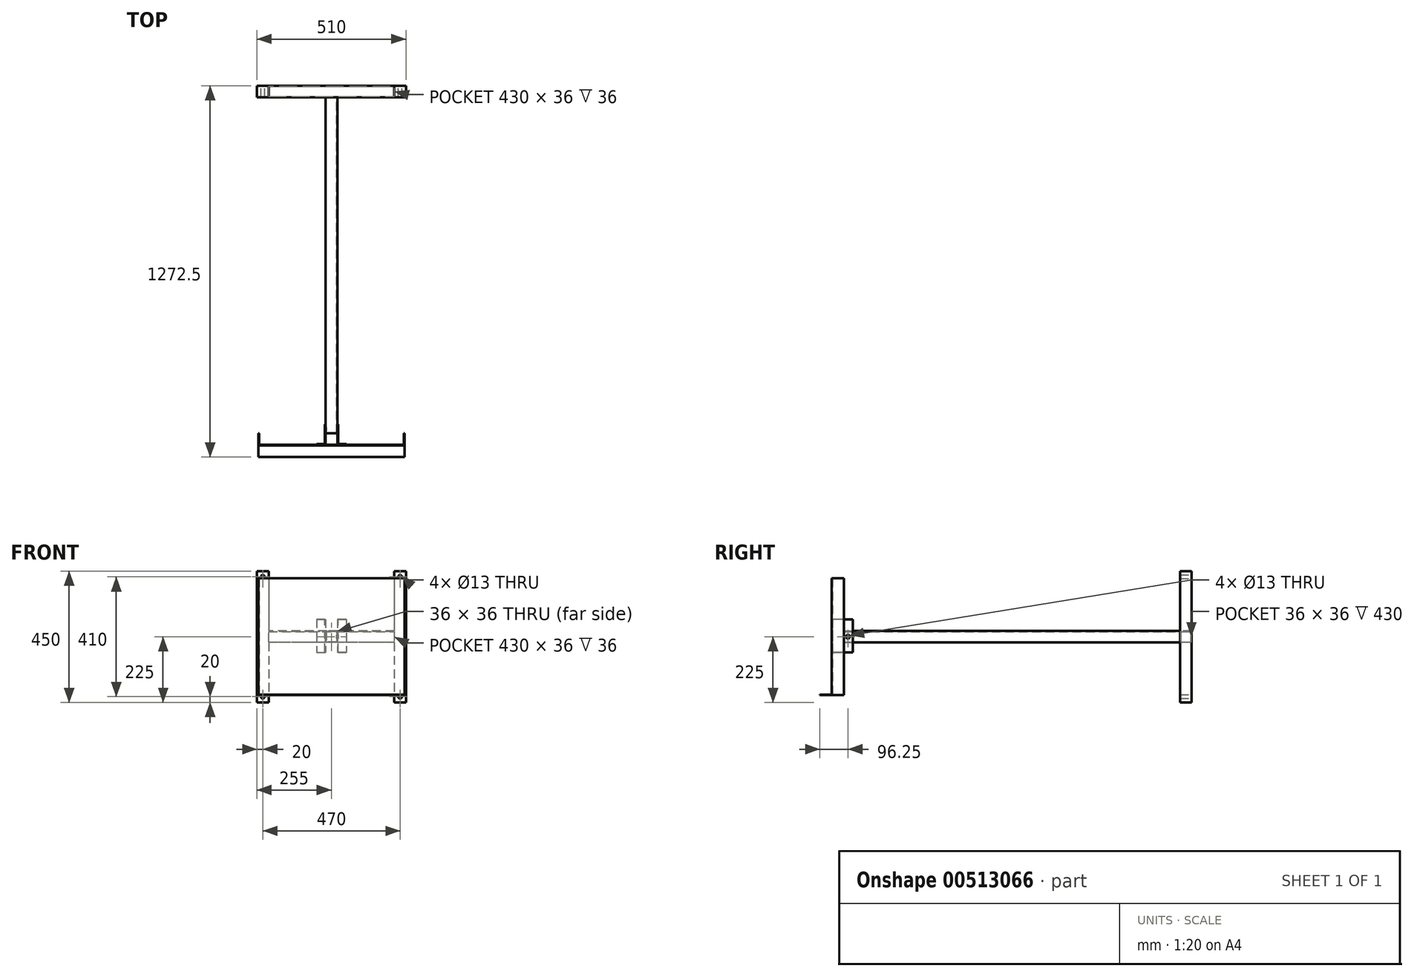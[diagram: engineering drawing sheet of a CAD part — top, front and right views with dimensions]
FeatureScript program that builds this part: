
annotation { "Feature Type Name" : "Feature", "Feature Type Description" : "" }
export const myFeature = defineFeature(function(context is Context, id is Id, definition is map)
    precondition{}
    {
        {
            var Q0;
            Q0=qCreatedBy(makeId("Front.planeOp"),FACE);
            var sketch = newSketch(context, id + "F0", { "sketchPlane" : qUnion([Q0])});
            skLineSegment(sketch, "E0.bottom", {"start": v(-250, 200) * mm, "end": v(250, 200) * mm});
            skLineSegment(sketch, "E0.top", {"start": v(-250, -200) * mm, "end": v(250, -200) * mm});
            skLineSegment(sketch, "E0.left", {"start": v(-250, 200) * mm, "end": v(-250, -200) * mm});
            skLineSegment(sketch, "E0.right", {"start": v(250, 200) * mm, "end": v(250, -200) * mm});
            skPoint(sketch, "E0.middle", {"position": v(0, 0) * mm});
            skSolve(sketch);
        }
        {
            var Q0;
            Q0 = qSketchRegion(id + "F0", true);
            extrude(context, id + "F1", {"entities" : qUnion([Q0]), "depth" : 2.5 * mm, "offsetDistance" : 25 * mm});
        }
        {
            var Q0;
            Q0=makeQuery(id+"F1.opExtrude","CAP_FACE",FACE,{"disambiguationData":[OSD([sQuery(id+"F0.wireOp",EDGE,"E0.bottom"),sQuery(id+"F0.wireOp",EDGE,"E0.top"),sQuery(id+"F0.wireOp",EDGE,"E0.left"),sQuery(id+"F0.wireOp",EDGE,"E0.right")])],"isStart":false});
            var sketch = newSketch(context, id + "F2", { "sketchPlane" : qUnion([Q0])});
            skLineSegment(sketch, "E1.bottom", {"start": v(-250, -198) * mm, "end": v(250, -198) * mm});
            skLineSegment(sketch, "E1.top", {"start": v(-250, -200) * mm, "end": v(250, -200) * mm});
            skLineSegment(sketch, "E1.left", {"start": v(-250, -198) * mm, "end": v(-250, -200) * mm});
            skLineSegment(sketch, "E1.right", {"start": v(250, -198) * mm, "end": v(250, -200) * mm});
            skSolve(sketch);
        }
        {
            var Q0;
            Q0=makeQuery(id+"F2.imprint","IMPRINT",FACE,{"disambiguationData":[TD([[makeQuery(id+"F2.imprint","IMPRINT",EDGE,{"derivedFrom":sQuery(id+"F2.wireOp",EDGE,"E1.bottom")}),-1.0]])]});
            extrude(context, id + "F3", {"entities" : qUnion([Q0]), "operationType" : NewBodyOperationType.ADD, "depth" : 40 * mm, "offsetDistance" : 25 * mm});
        }
        {
            var Q0;
            Q0=makeQuery(id+"F1.opExtrude","CAP_FACE",FACE,{"disambiguationData":[OSD([sQuery(id+"F0.wireOp",EDGE,"E0.bottom"),sQuery(id+"F0.wireOp",EDGE,"E0.top"),sQuery(id+"F0.wireOp",EDGE,"E0.left"),sQuery(id+"F0.wireOp",EDGE,"E0.right")])],"isStart":true});
            var sketch = newSketch(context, id + "F4", { "sketchPlane" : qUnion([Q0])});
            skLineSegment(sketch, "E2.bottom", {"start": v(-250, 200) * mm, "end": v(-248, 200) * mm});
            skLineSegment(sketch, "E2.top", {"start": v(-250, -200) * mm, "end": v(-248, -200) * mm});
            skLineSegment(sketch, "E2.left", {"start": v(-250, 200) * mm, "end": v(-250, -200) * mm});
            skLineSegment(sketch, "E2.right", {"start": v(-248, 200) * mm, "end": v(-248, -200) * mm});
            skLineSegment(sketch, "E3", {"start": v(0, 0) * mm, "end": v(0, 200) * mm, "construction": true});
            skLineSegment(sketch, "E4.MirrorCS", {"start": v(250, 200) * mm, "end": v(248, 200) * mm});
            skLineSegment(sketch, "E5.MirrorCS", {"start": v(250, -200) * mm, "end": v(248, -200) * mm});
            skLineSegment(sketch, "E6.MirrorCS", {"start": v(250, 200) * mm, "end": v(250, -200) * mm});
            skLineSegment(sketch, "E7.MirrorCS", {"start": v(248, 200) * mm, "end": v(248, -200) * mm});
            skSolve(sketch);
        }
        {
            var Q0;
            Q0=makeQuery(id+"F4.imprint","IMPRINT",FACE,{"disambiguationData":[TD([[makeQuery(id+"F4.imprint","IMPRINT",EDGE,{"derivedFrom":sQuery(id+"F4.wireOp",EDGE,"E2.bottom")}),1.0]])]});
            var Q1;
            Q1=makeQuery(id+"F4.imprint","IMPRINT",FACE,{"disambiguationData":[TD([[makeQuery(id+"F4.imprint","IMPRINT",EDGE,{"derivedFrom":sQuery(id+"F4.wireOp",EDGE,"E4.MirrorCS")}),1.0]])]});
            extrude(context, id + "F5", {"entities" : qUnion([Q0, Q1]), "operationType" : NewBodyOperationType.ADD, "depth" : 40 * mm, "offsetDistance" : 25 * mm});
        }
        {
            var Q0;
            Q0=makeQuery(id+"F1.opExtrude","CAP_FACE",FACE,{"disambiguationData":[OSD([sQuery(id+"F0.wireOp",EDGE,"E0.bottom"),sQuery(id+"F0.wireOp",EDGE,"E0.top"),sQuery(id+"F0.wireOp",EDGE,"E0.left"),sQuery(id+"F0.wireOp",EDGE,"E0.right")])],"isStart":true});
            var sketch = newSketch(context, id + "F6", { "sketchPlane" : qUnion([Q0])});
            skLineSegment(sketch, "E8", {"start": v(0, 224.2) * mm, "end": v(0, 0) * mm, "construction": true});
            skLineSegment(sketch, "E9", {"start": v(0, 0) * mm, "end": v(-292.5, 0) * mm, "construction": true});
            skLineSegment(sketch, "E10.bottom", {"start": v(-50.5, 60) * mm, "end": v(-20.5, 60) * mm});
            skLineSegment(sketch, "E10.top", {"start": v(-50.5, -53.15) * mm, "end": v(-20.5, -53.15) * mm});
            skLineSegment(sketch, "E10.left", {"start": v(-50.5, 60) * mm, "end": v(-50.5, -53.15) * mm});
            skLineSegment(sketch, "E10.right", {"start": v(-20.5, 60) * mm, "end": v(-20.5, -53.15) * mm});
            skLineSegment(sketch, "E11.MirrorCS", {"start": v(50.5, -53.15) * mm, "end": v(20.5, -53.15) * mm});
            skLineSegment(sketch, "E12.MirrorCS", {"start": v(50.5, 60) * mm, "end": v(20.5, 60) * mm});
            skLineSegment(sketch, "E13.MirrorCS", {"start": v(20.5, 60) * mm, "end": v(20.5, -53.15) * mm});
            skLineSegment(sketch, "E14.MirrorCS", {"start": v(50.5, 60) * mm, "end": v(50.5, -53.15) * mm});
            skSolve(sketch);
        }
        {
            var Q0;
            Q0=makeQuery(id+"F6.imprint","IMPRINT",FACE,{"disambiguationData":[TD([[makeQuery(id+"F6.imprint","IMPRINT",EDGE,{"derivedFrom":sQuery(id+"F6.wireOp",EDGE,"E10.bottom")}),-1.0]])]});
            var Q1;
            Q1=makeQuery(id+"F6.imprint","IMPRINT",FACE,{"disambiguationData":[TD([[makeQuery(id+"F6.imprint","IMPRINT",EDGE,{"derivedFrom":sQuery(id+"F6.wireOp",EDGE,"E11.MirrorCS")}),-1.0]])]});
            extrude(context, id + "F7", {"entities" : qUnion([Q0, Q1]), "operationType" : NewBodyOperationType.ADD, "depth" : 70 * mm, "offsetDistance" : 25 * mm});
        }
        {
            var Q0;
            Q0=makeQuery(id+"F7.opExtrude","SWEPT_FACE",FACE,{"disambiguationData":[OSD([sQuery(id+"F6.wireOp",EDGE,"E12.MirrorCS")])]});
            var sketch = newSketch(context, id + "F8", { "sketchPlane" : qUnion([Q0])});
            skLineSegment(sketch, "E15", {"start": v(0, 0) * mm, "end": v(0, 112.26) * mm, "construction": true});
            skLineSegment(sketch, "E16", {"start": v(-22.5, 70) * mm, "end": v(-22.5, 2) * mm});
            skLineSegment(sketch, "E17", {"start": v(-22.5, 2) * mm, "end": v(-50.5, 2) * mm});
            skLineSegment(sketch, "E18", {"start": v(-22.5, 70) * mm, "end": v(-20.5, 70) * mm});
            skLineSegment(sketch, "E19", {"start": v(-20.5, 70) * mm, "end": v(-20.5, 0) * mm});
            skLineSegment(sketch, "E20", {"start": v(-20.5, 0) * mm, "end": v(-50.5, 0) * mm});
            skLineSegment(sketch, "E21", {"start": v(-50.5, 0) * mm, "end": v(-50.5, 2) * mm});
            skLineSegment(sketch, "E22", {"start": v(-22.5, 70) * mm, "end": v(-50.5, 70) * mm});
            skLineSegment(sketch, "E23", {"start": v(-50.5, 70) * mm, "end": v(-50.5, 2) * mm});
            skLineSegment(sketch, "E24.MirrorCS", {"start": v(50.5, 0) * mm, "end": v(50.5, 2) * mm});
            skLineSegment(sketch, "E25.MirrorCS", {"start": v(22.5, 70) * mm, "end": v(20.5, 70) * mm});
            skLineSegment(sketch, "E26.MirrorCS", {"start": v(50.5, 70) * mm, "end": v(50.5, 2) * mm});
            skLineSegment(sketch, "E27.MirrorCS", {"start": v(22.5, 70) * mm, "end": v(50.5, 70) * mm});
            skLineSegment(sketch, "E28.MirrorCS", {"start": v(22.5, 70) * mm, "end": v(22.5, 2) * mm});
            skLineSegment(sketch, "E29.MirrorCS", {"start": v(20.5, 0) * mm, "end": v(50.5, 0) * mm});
            skLineSegment(sketch, "E30.MirrorCS", {"start": v(22.5, 2) * mm, "end": v(50.5, 2) * mm});
            skLineSegment(sketch, "E31.MirrorCS", {"start": v(20.5, 70) * mm, "end": v(20.5, 0) * mm});
            skSolve(sketch);
        }
        {
            var Q0;
            Q0=makeQuery(id+"F8.imprint","IMPRINT",FACE,{"disambiguationData":[TD([[makeQuery(id+"F8.imprint","IMPRINT",EDGE,{"derivedFrom":sQuery(id+"F8.wireOp",EDGE,"E26.MirrorCS")}),-1.0]])]});
            var Q1;
            Q1=makeQuery(id+"F8.imprint","IMPRINT",FACE,{"disambiguationData":[TD([[makeQuery(id+"F8.imprint","IMPRINT",EDGE,{"derivedFrom":sQuery(id+"F8.wireOp",EDGE,"E16")}),-1.0]])]});
            extrude(context, id + "F9", {"entities" : qUnion([Q0, Q1]), "operationType" : NewBodyOperationType.REMOVE, "endBound" : BoundingType.THROUGH_ALL, "oppositeDirection" : true, "depth" : 25 * mm, "offsetDistance" : 25 * mm});
        }
        {
            var Q0;
            Q0=qCreatedBy(makeId("Top.planeOp"),FACE);
            cPlane(context, id + "F10", {"entities" : qUnion([Q0]), "cplaneType" : CPlaneType.OFFSET, "offset" : 20 * mm, "width" : 150 * mm, "height" : 150 * mm});
        }
        {
            var Q0;
            Q0=qCreatedBy(id+"F10.planeOp",FACE);
            var sketch = newSketch(context, id + "F11", { "sketchPlane" : qUnion([Q0])});
            skLineSegment(sketch, "E32", {"start": v(0, 0) * mm, "end": v(0, -50.27) * mm, "construction": true});
            skLineSegment(sketch, "E33.bottom", {"start": v(0, 40) * mm, "end": v(20, 40) * mm});
            skLineSegment(sketch, "E33.top", {"start": v(0, 1190) * mm, "end": v(20, 1190) * mm});
            skLineSegment(sketch, "E33.right", {"start": v(20, 40) * mm, "end": v(20, 1190) * mm});
            skLineSegment(sketch, "E34.MirrorCS", {"start": v(-20, 40) * mm, "end": v(-20, 1190) * mm});
            skLineSegment(sketch, "E35.MirrorCS", {"start": v(0, 40) * mm, "end": v(-20, 40) * mm});
            skLineSegment(sketch, "E36.MirrorCS", {"start": v(0, 1190) * mm, "end": v(-20, 1190) * mm});
            skSolve(sketch);
        }
        {
            var Q0;
            Q0 = qSketchRegion(id + "F11", true);
            extrude(context, id + "F12", {"entities" : qUnion([Q0]), "oppositeDirection" : true, "depth" : 40 * mm, "offsetDistance" : 25 * mm});
        }
        {
            var Q0;
            Q0=makeQuery(id+"F12.opExtrude","SWEPT_FACE",FACE,{"disambiguationData":[OSD([sQuery(id+"F11.wireOp",EDGE,"E33.top"),sQuery(id+"F11.wireOp",EDGE,"E36.MirrorCS")])]});
            var sketch = newSketch(context, id + "F13", { "sketchPlane" : qUnion([Q0])});
            skLineSegment(sketch, "E37.bottom", {"start": v(-18, 18) * mm, "end": v(18, 18) * mm});
            skLineSegment(sketch, "E37.top", {"start": v(-18, -18) * mm, "end": v(18, -18) * mm});
            skLineSegment(sketch, "E37.left", {"start": v(-18, 18) * mm, "end": v(-18, -18) * mm});
            skLineSegment(sketch, "E37.right", {"start": v(18, 18) * mm, "end": v(18, -18) * mm});
            skPoint(sketch, "E37.middle", {"position": v(0, 0) * mm});
            skSolve(sketch);
        }
        {
            var Q0;
            Q0=makeQuery(id+"F13.imprint","IMPRINT",FACE,{"disambiguationData":[TD([[makeQuery(id+"F13.imprint","IMPRINT",EDGE,{"derivedFrom":sQuery(id+"F13.wireOp",EDGE,"E37.bottom")}),-1.0]])]});
            extrude(context, id + "F14", {"entities" : qUnion([Q0]), "operationType" : NewBodyOperationType.REMOVE, "oppositeDirection" : true, "depth" : 1151 * mm, "offsetDistance" : 25 * mm});
        }
        {
            var Q0;
            Q0=makeQuery(id+"F9.boolean.opBoolean","COPY",FACE,{"derivedFrom":makeQuery(id+"F9.opExtrude","SWEPT_FACE",FACE,{"disambiguationData":[OSD([sQuery(id+"F8.wireOp",EDGE,"E16")])]})});
            var sketch = newSketch(context, id + "F15", { "sketchPlane" : qUnion([Q0])});
            skLineSegment(sketch, "E38.bottom", {"start": v(-70, 20) * mm, "end": v(2.5, 20) * mm});
            skLineSegment(sketch, "E38.left", {"start": v(2.5, 20) * mm, "end": v(2.5, 0) * mm});
            skLineSegment(sketch, "E38.right", {"start": v(-70, 20) * mm, "end": v(-70, 0) * mm});
            skLineSegment(sketch, "E39.MirrorCS", {"start": v(-30, -20) * mm, "end": v(-37.5, -20) * mm});
            skLineSegment(sketch, "E40", {"start": v(0, 0) * mm, "end": v(-67.93, 0) * mm, "construction": true});
            skLineSegment(sketch, "E41.MirrorCS", {"start": v(-70, -20) * mm, "end": v(-70, 0) * mm});
            skLineSegment(sketch, "E42.MirrorCS", {"start": v(2.5, -20) * mm, "end": v(2.5, 0) * mm});
            skLineSegment(sketch, "E43", {"start": v(-70, 20) * mm, "end": v(-37.5, -20) * mm});
            skLineSegment(sketch, "E44", {"start": v(2.5, 20) * mm, "end": v(-30, -20) * mm});
            skPoint(sketch, "E45", {"position": v(-53.75, 0) * mm});
            skSolve(sketch);
        }
        {
            var Q0;
            Q0=sQuery(id+"F15.wireOp",VERTEX,"E45");
            var Q1;
            Q1=makeQuery(id+"F1.opExtrude","SWEPT_BODY",BODY,{"disambiguationData":[OSD([sQuery(id+"F0.wireOp",EDGE,"E0.bottom"),sQuery(id+"F0.wireOp",EDGE,"E0.top"),sQuery(id+"F0.wireOp",EDGE,"E0.left"),sQuery(id+"F0.wireOp",EDGE,"E0.right")])]});
            var Q2;
            Q2=makeQuery(id+"F12.opExtrude","SWEPT_BODY",BODY,{"disambiguationData":[OSD([sQuery(id+"F11.wireOp",EDGE,"E33.bottom"),sQuery(id+"F11.wireOp",EDGE,"E33.top"),sQuery(id+"F11.wireOp",EDGE,"E33.right"),sQuery(id+"F11.wireOp",EDGE,"E34.MirrorCS"),sQuery(id+"F11.wireOp",EDGE,"E35.MirrorCS"),sQuery(id+"F11.wireOp",EDGE,"E36.MirrorCS")])]});
            hole(context, id + "F16", {"style" : HoleStyle.SIMPLE, "endStyle" : HoleEndStyle.BLIND, "holeDiameter" : 13 * mm, "holeDepth" : 50 * mm, "isTappedThrough" : true, "tappedDepth" : 12 * mm, "tapClearance" : 3, "startFromSketch" : true, "locations" : qUnion([Q0]), "scope" : qUnion([Q1, Q2])});
        }
        {
            var Q0;
            Q0=makeQuery(id+"F12.opExtrude","SWEPT_FACE",FACE,{"disambiguationData":[OSD([sQuery(id+"F11.wireOp",EDGE,"E33.top"),sQuery(id+"F11.wireOp",EDGE,"E36.MirrorCS")])]});
            cPlane(context, id + "F17", {"entities" : qUnion([Q0]), "cplaneType" : CPlaneType.OFFSET, "offset" : 0 * mm, "width" : 150 * mm, "height" : 150 * mm});
        }
        {
            var Q0;
            Q0=qCreatedBy(id+"F17.planeOp",FACE);
            var sketch = newSketch(context, id + "F18", { "sketchPlane" : qUnion([Q0])});
            skLineSegment(sketch, "E46.bottom", {"start": v(-215, 20) * mm, "end": v(215, 20) * mm});
            skLineSegment(sketch, "E46.top", {"start": v(-215, -20) * mm, "end": v(215, -20) * mm});
            skLineSegment(sketch, "E46.left", {"start": v(-215, 20) * mm, "end": v(-215, -20) * mm});
            skLineSegment(sketch, "E46.right", {"start": v(215, 20) * mm, "end": v(215, -20) * mm});
            skPoint(sketch, "E46.middle", {"position": v(0, 0) * mm});
            skSolve(sketch);
        }
        {
            var Q0;
            Q0=makeQuery(id+"F18.imprint","IMPRINT",FACE,{"disambiguationData":[TD([[makeQuery(id+"F18.imprint","IMPRINT",EDGE,{"derivedFrom":sQuery(id+"F18.wireOp",EDGE,"E46.bottom")}),-1.0]])]});
            extrude(context, id + "F19", {"entities" : qUnion([Q0]), "depth" : 40 * mm, "offsetDistance" : 25 * mm});
        }
        {
            var Q0;
            Q0=makeQuery(id+"F19.opExtrude","SWEPT_FACE",FACE,{"disambiguationData":[OSD([sQuery(id+"F18.wireOp",EDGE,"E46.left")])]});
            var sketch = newSketch(context, id + "F20", { "sketchPlane" : qUnion([Q0])});
            skLineSegment(sketch, "E47", {"start": v(1190, 20) * mm, "end": v(1230, -20) * mm});
            skLineSegment(sketch, "E48", {"start": v(1230, 20) * mm, "end": v(1190, -20) * mm});
            skPoint(sketch, "E49", {"position": v(1210, 0) * mm});
            skLineSegment(sketch, "E50.bottom", {"start": v(1192, 18) * mm, "end": v(1228, 18) * mm});
            skLineSegment(sketch, "E50.top", {"start": v(1192, -18) * mm, "end": v(1228, -18) * mm});
            skLineSegment(sketch, "E50.left", {"start": v(1192, 18) * mm, "end": v(1192, -18) * mm});
            skLineSegment(sketch, "E50.right", {"start": v(1228, 18) * mm, "end": v(1228, -18) * mm});
            skSolve(sketch);
        }
        {
            var Q0;
            {var subQ0=sQuery(id+"F20.wireOp",EDGE,"E50.bottom");Q0=makeQuery(id+"F20.imprint","IMPRINT",FACE,{"disambiguationData":[TD([[makeQuery(id+"F20.imprint","IMPRINT",EDGE,{"derivedFrom":subQ0}),-1.0]])]});}
            var Q1;
            {var subQ0=sQuery(id+"F20.wireOp",EDGE,"E50.left");Q1=makeQuery(id+"F20.imprint","IMPRINT",FACE,{"disambiguationData":[TD([[makeQuery(id+"F20.imprint","IMPRINT",EDGE,{"derivedFrom":subQ0}),1.0]])]});}
            var Q2;
            {var subQ0=sQuery(id+"F20.wireOp",EDGE,"E50.top");Q2=makeQuery(id+"F20.imprint","IMPRINT",FACE,{"disambiguationData":[TD([[makeQuery(id+"F20.imprint","IMPRINT",EDGE,{"derivedFrom":subQ0}),1.0]])]});}
            var Q3;
            {var subQ0=sQuery(id+"F20.wireOp",EDGE,"E50.right");Q3=makeQuery(id+"F20.imprint","IMPRINT",FACE,{"disambiguationData":[TD([[makeQuery(id+"F20.imprint","IMPRINT",EDGE,{"derivedFrom":subQ0}),-1.0]])]});}
            extrude(context, id + "F21", {"entities" : qUnion([Q0, Q1, Q2, Q3]), "operationType" : NewBodyOperationType.REMOVE, "endBound" : BoundingType.THROUGH_ALL, "oppositeDirection" : true, "depth" : 25 * mm, "offsetDistance" : 25 * mm});
        }
        {
            var Q0;
            Q0=makeQuery(id+"F19.opExtrude","SWEPT_FACE",FACE,{"disambiguationData":[OSD([sQuery(id+"F18.wireOp",EDGE,"E46.left")])]});
            cPlane(context, id + "F22", {"entities" : qUnion([Q0]), "cplaneType" : CPlaneType.OFFSET, "offset" : 0 * mm, "width" : 150 * mm, "height" : 150 * mm});
        }
        {
            var Q0;
            Q0=qCreatedBy(id+"F22.planeOp",FACE);
            var sketch = newSketch(context, id + "F23", { "sketchPlane" : qUnion([Q0])});
            skPoint(sketch, "E51", {"position": v(1210, 0) * mm});
            skLineSegment(sketch, "E52.bottom", {"start": v(1190, 225) * mm, "end": v(1230, 225) * mm});
            skLineSegment(sketch, "E52.top", {"start": v(1190, -225) * mm, "end": v(1230, -225) * mm});
            skLineSegment(sketch, "E52.left", {"start": v(1190, 225) * mm, "end": v(1190, -225) * mm});
            skLineSegment(sketch, "E52.right", {"start": v(1230, 225) * mm, "end": v(1230, -225) * mm});
            skPoint(sketch, "E53.orphan", {"position": v(1230, 20) * mm});
            skPoint(sketch, "E54.end.orphan", {"position": v(1190, -20) * mm});
            skSolve(sketch);
        }
        {
            var Q0;
            Q0 = qSketchRegion(id + "F23", true);
            extrude(context, id + "F24", {"entities" : qUnion([Q0]), "depth" : 40 * mm, "offsetDistance" : 25 * mm});
        }
        {
            var Q0;
            Q0=makeQuery(id+"F24.opExtrude","SWEPT_BODY",BODY,{"disambiguationData":[OSD([sQuery(id+"F23.wireOp",EDGE,"E52.bottom"),sQuery(id+"F23.wireOp",EDGE,"E52.top"),sQuery(id+"F23.wireOp",EDGE,"E52.left"),sQuery(id+"F23.wireOp",EDGE,"E52.right")])]});
            var Q1;
            Q1=qCreatedBy(makeId("Right.planeOp"),FACE);
            mirror(context, id + "F25", {"operationType" : NewBodyOperationType.ADD, "entities" : qUnion([Q0]), "mirrorPlane" : qUnion([Q1])});
        }
        {
            var Q0;
            {var subQ0=makeQuery(id+"F24.opExtrude","SWEPT_FACE",FACE,{"disambiguationData":[OSD([sQuery(id+"F23.wireOp",EDGE,"E52.right")])]});Q0=makeQuery(id+"F25.boolean.opBoolean","MERGE",FACE,{"derivedFrom":[makeQuery(id+"F19.opExtrude","CAP_FACE",FACE,{"disambiguationData":[OSD([sQuery(id+"F18.wireOp",EDGE,"E46.bottom"),sQuery(id+"F18.wireOp",EDGE,"E46.top"),sQuery(id+"F18.wireOp",EDGE,"E46.left"),sQuery(id+"F18.wireOp",EDGE,"E46.right")])],"isStart":false}),subQ0,makeQuery(id+"F25.opPattern","COPY",FACE,{"derivedFrom":subQ0,"instanceName":"1"})]});}
            var sketch = newSketch(context, id + "F26", { "sketchPlane" : qUnion([Q0])});
            skLineSegment(sketch, "E55.bottom", {"start": v(-255, 225) * mm, "end": v(-215, 225) * mm});
            skLineSegment(sketch, "E55.top", {"start": v(-255, 185) * mm, "end": v(-215, 185) * mm});
            skLineSegment(sketch, "E55.left", {"start": v(-255, 225) * mm, "end": v(-255, 185) * mm});
            skLineSegment(sketch, "E55.right", {"start": v(-215, 225) * mm, "end": v(-215, 185) * mm});
            skLineSegment(sketch, "E56", {"start": v(0, 254.48) * mm, "end": v(0, 0) * mm, "construction": true});
            skLineSegment(sketch, "E57", {"start": v(0, 0) * mm, "end": v(-392.92, 0) * mm, "construction": true});
            skLineSegment(sketch, "E58.MirrorCS", {"start": v(255, 185) * mm, "end": v(215, 185) * mm});
            skLineSegment(sketch, "E59.MirrorCS", {"start": v(255, 225) * mm, "end": v(215, 225) * mm});
            skLineSegment(sketch, "E60.MirrorCS", {"start": v(255, 225) * mm, "end": v(255, 185) * mm});
            skLineSegment(sketch, "E61.MirrorCS", {"start": v(215, 225) * mm, "end": v(215, 185) * mm});
            skLineSegment(sketch, "E62.MirrorCS", {"start": v(215, -225) * mm, "end": v(215, -185) * mm});
            skLineSegment(sketch, "E63.MirrorCS", {"start": v(255, -225) * mm, "end": v(255, -185) * mm});
            skLineSegment(sketch, "E64.MirrorCS", {"start": v(255, -225) * mm, "end": v(215, -225) * mm});
            skLineSegment(sketch, "E65.MirrorCS", {"start": v(255, -185) * mm, "end": v(215, -185) * mm});
            skLineSegment(sketch, "E66.MirrorCS", {"start": v(-255, -225) * mm, "end": v(-215, -225) * mm});
            skLineSegment(sketch, "E67.MirrorCS", {"start": v(-215, -225) * mm, "end": v(-215, -185) * mm});
            skLineSegment(sketch, "E68.MirrorCS", {"start": v(-255, -185) * mm, "end": v(-215, -185) * mm});
            skLineSegment(sketch, "E69.MirrorCS", {"start": v(-255, -225) * mm, "end": v(-255, -185) * mm});
            skLineSegment(sketch, "E70", {"start": v(-255, 225) * mm, "end": v(-215, 185) * mm});
            skLineSegment(sketch, "E71", {"start": v(-215, 225) * mm, "end": v(-255, 185) * mm});
            skPoint(sketch, "E72", {"position": v(-235, 205) * mm});
            skPoint(sketch, "E73.MirrorP", {"position": v(235, 205) * mm});
            skPoint(sketch, "E74.MirrorP", {"position": v(-235, -205) * mm});
            skPoint(sketch, "E75.MirrorP", {"position": v(235, -205) * mm});
            skSolve(sketch);
        }
        {
            var Q0;
            Q0=sQuery(id+"F26.wireOp",VERTEX,"E72");
            var Q1;
            Q1=sQuery(id+"F26.wireOp",VERTEX,"E73.MirrorP");
            var Q2;
            Q2=sQuery(id+"F26.wireOp",VERTEX,"E75.MirrorP");
            var Q3;
            Q3=sQuery(id+"F26.wireOp",VERTEX,"E74.MirrorP");
            var Q4;
            Q4=makeQuery(id+"F19.opExtrude","SWEPT_BODY",BODY,{"disambiguationData":[OSD([sQuery(id+"F18.wireOp",EDGE,"E46.bottom"),sQuery(id+"F18.wireOp",EDGE,"E46.top"),sQuery(id+"F18.wireOp",EDGE,"E46.left"),sQuery(id+"F18.wireOp",EDGE,"E46.right")])]});
            hole(context, id + "F27", {"style" : HoleStyle.SIMPLE, "endStyle" : HoleEndStyle.BLIND, "holeDiameter" : 13 * mm, "holeDepth" : 50 * mm, "isTappedThrough" : true, "tappedDepth" : 12 * mm, "tapClearance" : 3, "startFromSketch" : true, "locations" : qUnion([Q0, Q1, Q2, Q3]), "scope" : qUnion([Q4])});
        }
    });
